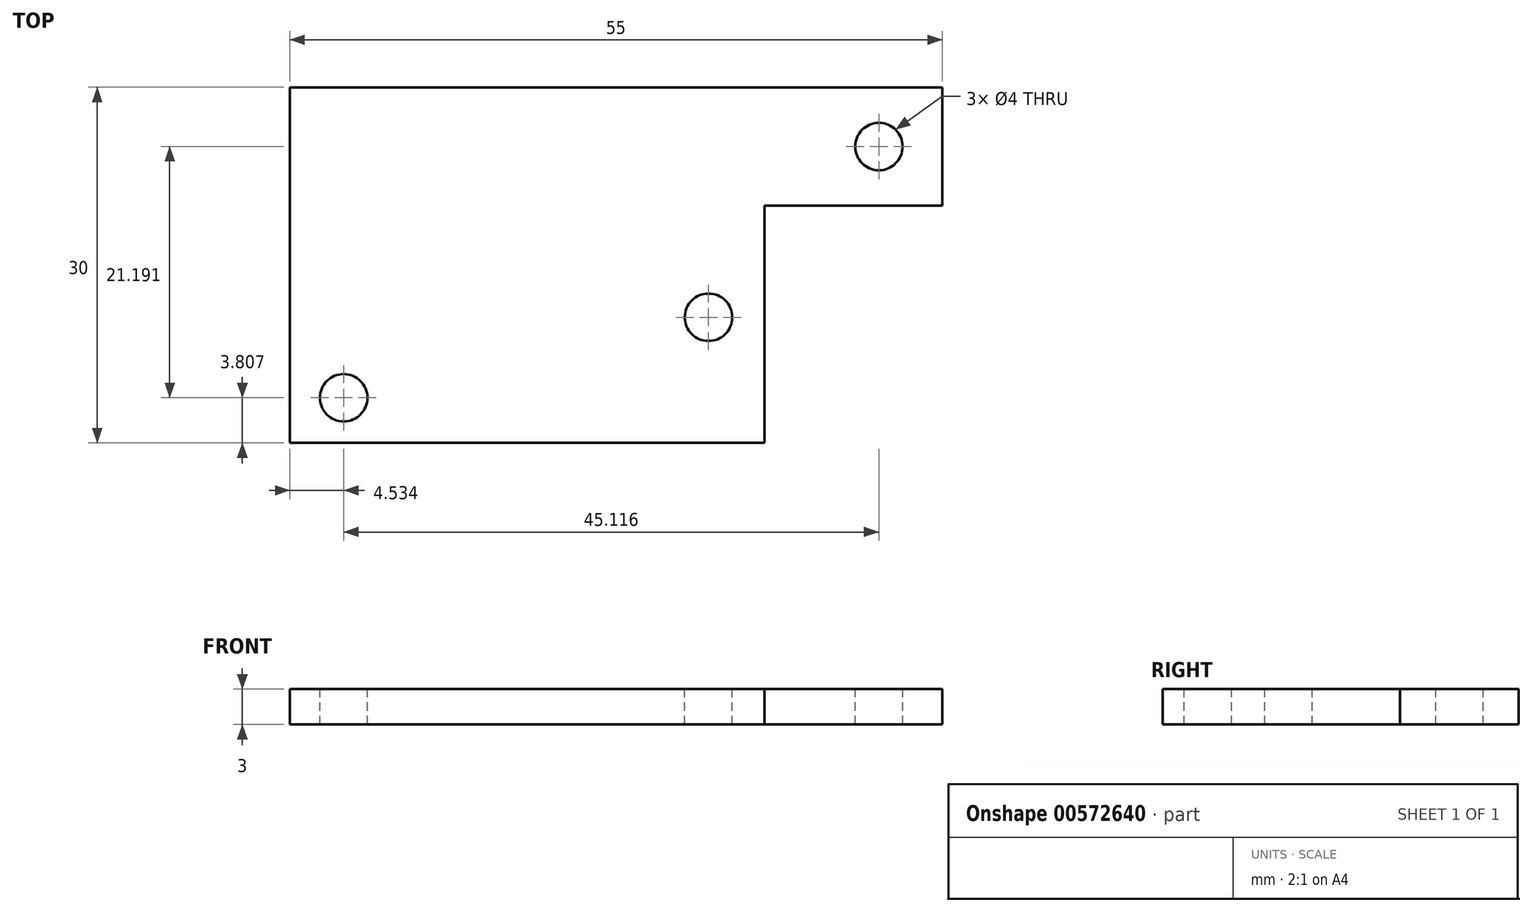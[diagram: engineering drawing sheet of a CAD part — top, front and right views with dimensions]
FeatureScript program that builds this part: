
annotation { "Feature Type Name" : "Feature", "Feature Type Description" : "" }
export const myFeature = defineFeature(function(context is Context, id is Id, definition is map)
    precondition{}
    {
        {
            var Q0;
            Q0=qCreatedBy(makeId("Top.planeOp"),FACE);
            var sketch = newSketch(context, id + "F0", { "sketchPlane" : qUnion([Q0])});
            skLineSegment(sketch, "E0", {"start": v(-49.65, -20.41) * mm, "end": v(-49.65, 9.59) * mm});
            skLineSegment(sketch, "E1", {"start": v(-49.65, 9.59) * mm, "end": v(5.35, 9.59) * mm});
            skLineSegment(sketch, "E2", {"start": v(5.35, 9.59) * mm, "end": v(5.35, -0.41) * mm});
            skLineSegment(sketch, "E3", {"start": v(5.35, -0.41) * mm, "end": v(-9.65, -0.41) * mm});
            skLineSegment(sketch, "E4", {"start": v(-49.65, -20.41) * mm, "end": v(-9.65, -20.41) * mm});
            skLineSegment(sketch, "E5", {"start": v(-9.65, -20.41) * mm, "end": v(-9.65, -0.41) * mm});
            skSolve(sketch);
        }
        {
            var Q0;
            Q0 = qSketchRegion(id + "F0", true);
            extrude(context, id + "F1", {"entities" : qUnion([Q0]), "depth" : 3 * mm, "offsetDistance" : 25 * mm});
        }
        {
            var Q0;
            Q0=makeQuery(id+"F1.opExtrude","CAP_FACE",FACE,{"disambiguationData":[OSD([sQuery(id+"F0.wireOp",EDGE,"E0"),sQuery(id+"F0.wireOp",EDGE,"E1"),sQuery(id+"F0.wireOp",EDGE,"E2"),sQuery(id+"F0.wireOp",EDGE,"E3"),sQuery(id+"F0.wireOp",EDGE,"E4"),sQuery(id+"F0.wireOp",EDGE,"E5")])],"isStart":false});
            var sketch = newSketch(context, id + "F2", { "sketchPlane" : qUnion([Q0])});
            skPoint(sketch, "E6", {"position": v(0, 4.59) * mm});
            skPoint(sketch, "E7", {"position": v(-14.36, -9.81) * mm});
            skPoint(sketch, "E8", {"position": v(-45.12, -16.6) * mm});
            skPoint(sketch, "E9", {"position": v(5.35, 4.59) * mm});
            skSolve(sketch);
        }
        {
            var Q0;
            Q0=sQuery(id+"F2.wireOp",VERTEX,"E8");
            var Q1;
            Q1=sQuery(id+"F2.wireOp",VERTEX,"E7");
            var Q2;
            Q2=sQuery(id+"F2.wireOp",VERTEX,"E6");
            var Q3;
            Q3=makeQuery(id+"F1.opExtrude","SWEPT_BODY",BODY,{"disambiguationData":[OSD([sQuery(id+"F0.wireOp",EDGE,"E0"),sQuery(id+"F0.wireOp",EDGE,"E1"),sQuery(id+"F0.wireOp",EDGE,"E2"),sQuery(id+"F0.wireOp",EDGE,"E3"),sQuery(id+"F0.wireOp",EDGE,"E4"),sQuery(id+"F0.wireOp",EDGE,"E5")])]});
            hole(context, id + "F3", {"style" : HoleStyle.SIMPLE, "endStyle" : HoleEndStyle.THROUGH, "holeDiameter" : 4 * mm, "isTappedThrough" : true, "tappedDepth" : 12 * mm, "tapClearance" : 3, "locations" : qUnion([Q0, Q1, Q2]), "scope" : qUnion([Q3])});
        }
    });
